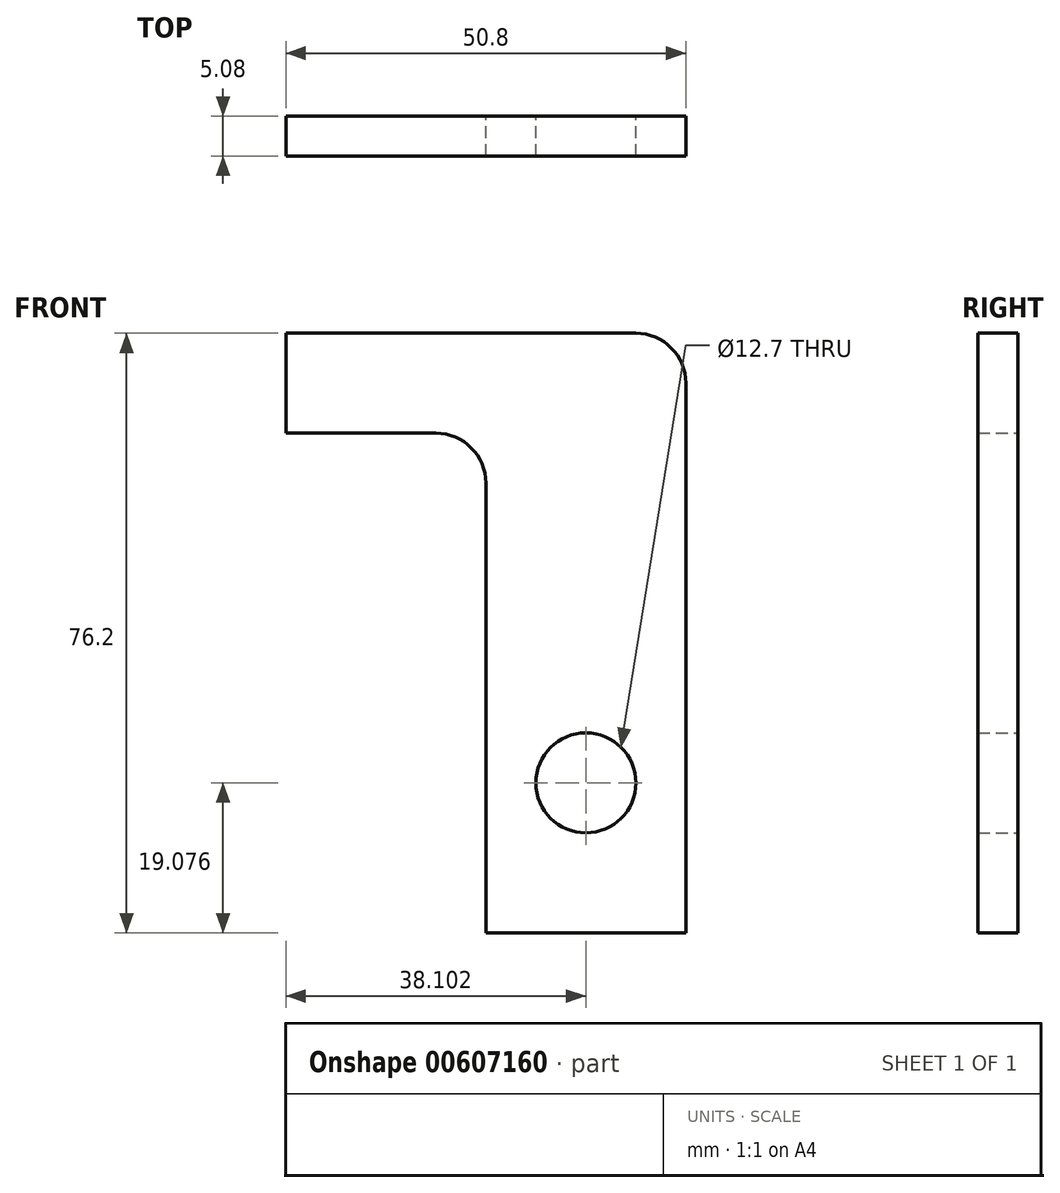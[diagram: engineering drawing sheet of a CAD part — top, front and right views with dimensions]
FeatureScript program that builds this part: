
annotation { "Feature Type Name" : "Feature", "Feature Type Description" : "" }
export const myFeature = defineFeature(function(context is Context, id is Id, definition is map)
    precondition{}
    {
        {
            var Q0;
            Q0=qCreatedBy(makeId("Front.planeOp"),FACE);
            var sketch = newSketch(context, id + "F0", { "sketchPlane" : qUnion([Q0])});
            skLineSegment(sketch, "E0.bottom", {"start": v(-45.5, 45.92) * mm, "end": v(-20.1, 45.92) * mm});
            skLineSegment(sketch, "E0.top", {"start": v(-45.5, 33.22) * mm, "end": v(-26.46, 33.22) * mm});
            skLineSegment(sketch, "E0.left", {"start": v(-45.5, 45.92) * mm, "end": v(-45.5, 33.22) * mm});
            skLineSegment(sketch, "E0.right", {"start": v(-20.1, 45.92) * mm, "end": v(-20.1, 33.22) * mm});
            skLineSegment(sketch, "E1.bottom", {"start": v(-20.1, 45.92) * mm, "end": v(-1.06, 45.92) * mm});
            skLineSegment(sketch, "E1.top", {"start": v(-20.1, -30.28) * mm, "end": v(5.3, -30.28) * mm});
            skLineSegment(sketch, "E1.left", {"start": v(-20.1, 26.87) * mm, "end": v(-20.1, -30.28) * mm});
            skLineSegment(sketch, "E1.right", {"start": v(5.3, 39.57) * mm, "end": v(5.3, -30.28) * mm});
            skCircle(sketch, "E2", {"center": v(-7.4, -11.2) * mm, "radius": 6.35 * mm});
            skLineSegment(sketch, "E3", {"start": v(-7.92, -4.88) * mm, "end": v(-7.92, 45.92) * mm});
            skArc(sketch, "E4.filletArc", {"start": v(-20.1, 26.87) * mm, "mid": v(-21.97, 31.37) * mm, "end": v(-26.46, 33.22) * mm});
            skPoint(sketch, "E5.visualSharp", {"position": v(5.3, 45.92) * mm});
            skArc(sketch, "E5.filletArc", {"start": v(5.3, 39.57) * mm, "mid": v(3.43, 44.07) * mm, "end": v(-1.06, 45.92) * mm});
            skSolve(sketch);
        }
        {
            var Q0;
            Q0 = qSketchRegion(id + "F0", true);
            extrude(context, id + "F1", {"entities" : qUnion([Q0]), "depth" : 5.08 * mm, "offsetDistance" : 25.4 * mm});
        }
    });
